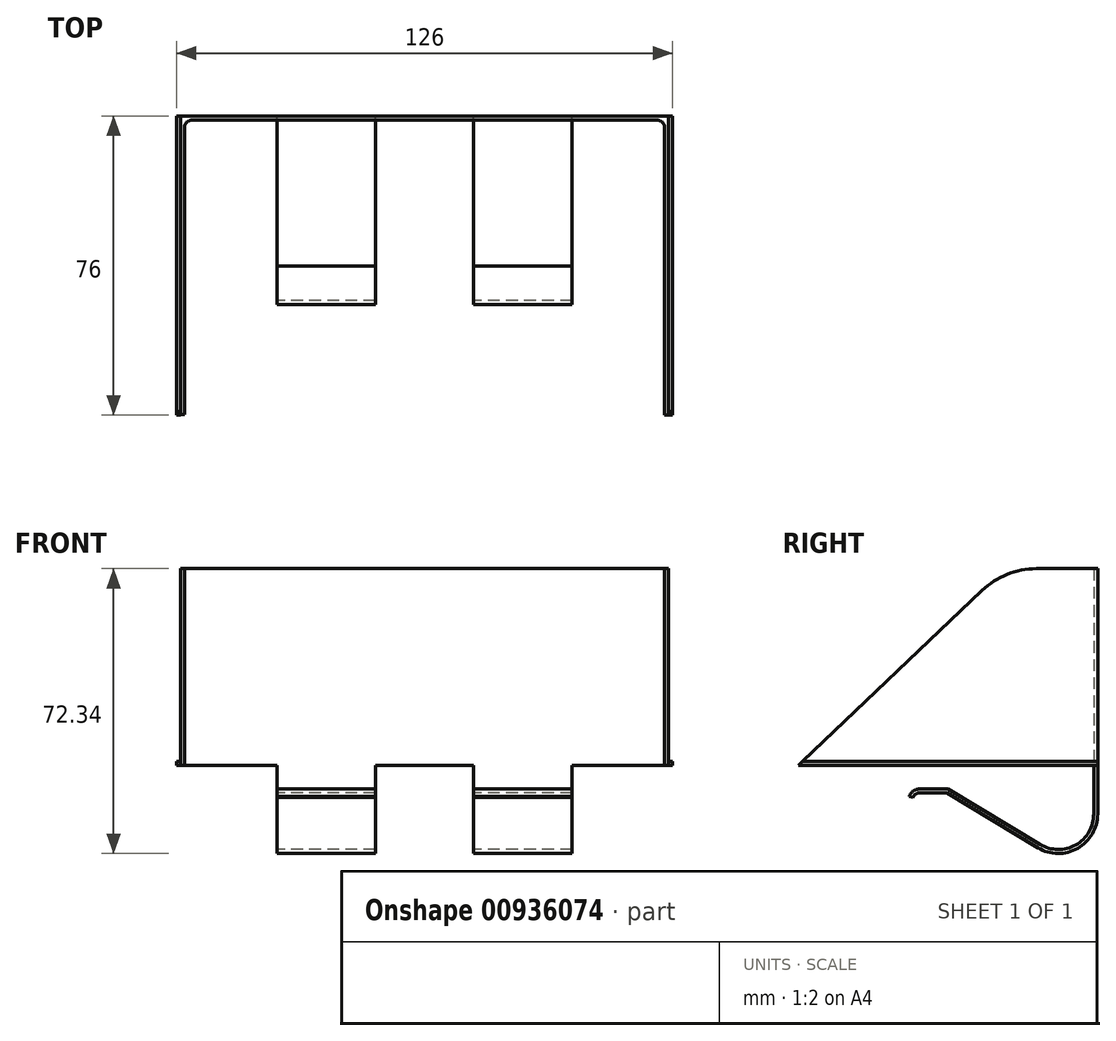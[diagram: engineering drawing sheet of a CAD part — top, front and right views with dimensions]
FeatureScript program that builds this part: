
annotation { "Feature Type Name" : "Feature", "Feature Type Description" : "" }
export const myFeature = defineFeature(function(context is Context, id is Id, definition is map)
    precondition{}
    {
        {
            var Q0;
            Q0=qCreatedBy(makeId("Top.planeOp"),FACE);
            var sketch = newSketch(context, id + "F0", { "sketchPlane" : qUnion([Q0])});
            skLineSegment(sketch, "E0", {"start": v(0, 0) * mm, "end": v(59, 0) * mm});
            skLineSegment(sketch, "E1", {"start": v(0, 0) * mm, "end": v(-59, 0) * mm});
            skLineSegment(sketch, "E2", {"start": v(-61, -2) * mm, "end": v(-61, -75) * mm});
            skLineSegment(sketch, "E3", {"start": v(61, -2) * mm, "end": v(61, -75) * mm});
            skLineSegment(sketch, "E4.0", {"start": v(62, 1) * mm, "end": v(62, -75) * mm});
            skLineSegment(sketch, "E5.0", {"start": v(0, 1) * mm, "end": v(63, 1) * mm});
            skLineSegment(sketch, "E6.0", {"start": v(0, 1) * mm, "end": v(-63, 1) * mm});
            skLineSegment(sketch, "E7.0", {"start": v(-62, 1) * mm, "end": v(-62, -75) * mm});
            skPoint(sketch, "E8.visualSharp", {"position": v(-61, 0) * mm});
            skArc(sketch, "E8.filletArc", {"start": v(-59, 0) * mm, "mid": v(-60.41, -0.59) * mm, "end": v(-61, -2) * mm});
            skPoint(sketch, "E9.visualSharp", {"position": v(61, 0) * mm});
            skArc(sketch, "E9.filletArc", {"start": v(61, -2) * mm, "mid": v(60.41, -0.59) * mm, "end": v(59, 0) * mm});
            skLineSegment(sketch, "E10", {"start": v(61, -75) * mm, "end": v(62, -75) * mm});
            skLineSegment(sketch, "E11", {"start": v(-62, -75) * mm, "end": v(-61, -75) * mm});
            skLineSegment(sketch, "E12", {"start": v(-62, -22.58) * mm, "end": v(-61, -22.58) * mm});
            skLineSegment(sketch, "E13", {"start": v(61, -22.58) * mm, "end": v(62, -22.58) * mm});
            skLineSegment(sketch, "E14", {"start": v(-62, -75) * mm, "end": v(-63, -75) * mm});
            skLineSegment(sketch, "E15", {"start": v(-63, -75) * mm, "end": v(-63, 1) * mm});
            skPoint(sketch, "E16.orphan", {"position": v(-63, 0) * mm});
            skLineSegment(sketch, "E17", {"start": v(62, -75) * mm, "end": v(63, -75) * mm});
            skLineSegment(sketch, "E18", {"start": v(63, -75) * mm, "end": v(63, 1) * mm});
            skPoint(sketch, "E19.orphan", {"position": v(60, 1) * mm});
            skSolve(sketch);
        }
        {
            var Q0;
            Q0=makeQuery(id+"F0.imprint","IMPRINT",FACE,{"disambiguationData":[TD([[makeQuery(id+"F0.imprint","IMPRINT",EDGE,{"derivedFrom":sQuery(id+"F0.wireOp",EDGE,"E0")}),1.0]])]});
            extrude(context, id + "F1", {"entities" : qUnion([Q0]), "depth" : 50 * mm, "offsetDistance" : 25 * mm});
        }
        {
            var Q0;
            Q0=makeQuery(id+"F1.opExtrude","SWEPT_FACE",FACE,{"disambiguationData":[OSD([sQuery(id+"F0.wireOp",EDGE,"E7.0")])]});
            var sketch = newSketch(context, id + "F2", { "sketchPlane" : qUnion([Q0])});
            skLineSegment(sketch, "E20", {"start": v(22.58, 50) * mm, "end": v(74.85, 0) * mm});
            skLineSegment(sketch, "E21", {"start": v(74.85, 0) * mm, "end": v(22.58, 0) * mm});
            skSolve(sketch);
        }
        {
            var Q0;
            Q0=makeQuery(id+"F2.imprint","IMPRINT",FACE,{"disambiguationData":[TD([[makeQuery(id+"F2.imprint","IMPRINT",EDGE,{"derivedFrom":sQuery(id+"F2.wireOp",EDGE,"E20")}),-1.0]])]});
            extrude(context, id + "F3", {"entities" : qUnion([Q0]), "operationType" : NewBodyOperationType.ADD, "oppositeDirection" : true, "depth" : 1 * mm, "offsetDistance" : 25 * mm});
        }
        {
            var Q0;
            Q0=makeQuery(id+"F1.opExtrude","SWEPT_FACE",FACE,{"disambiguationData":[OSD([sQuery(id+"F0.wireOp",EDGE,"E4.0")])]});
            var sketch = newSketch(context, id + "F4", { "sketchPlane" : qUnion([Q0])});
            skLineSegment(sketch, "E22", {"start": v(-22.58, 50) * mm, "end": v(-74.98, 0) * mm});
            skLineSegment(sketch, "E23", {"start": v(-74.98, 0) * mm, "end": v(-22.58, 0) * mm});
            skSolve(sketch);
        }
        {
            var Q0;
            Q0=makeQuery(id+"F4.imprint","IMPRINT",FACE,{"disambiguationData":[TD([[makeQuery(id+"F4.imprint","IMPRINT",EDGE,{"derivedFrom":sQuery(id+"F4.wireOp",EDGE,"E22")}),1.0]])]});
            extrude(context, id + "F5", {"entities" : qUnion([Q0]), "operationType" : NewBodyOperationType.ADD, "oppositeDirection" : true, "depth" : 1 * mm, "offsetDistance" : 25 * mm});
        }
        {
            var Q0;
            {var subQ4=sQuery(id+"F0.wireOp",EDGE,"E17");Q0=makeQuery(id+"F0.imprint","IMPRINT",FACE,{"disambiguationData":[TD([[makeQuery(id+"F0.imprint","IMPRINT",EDGE,{"derivedFrom":subQ4}),1.0]])]});}
            var Q1;
            {var subQ0=sQuery(id+"F0.wireOp",EDGE,"E14");Q1=makeQuery(id+"F0.imprint","IMPRINT",FACE,{"disambiguationData":[TD([[makeQuery(id+"F0.imprint","IMPRINT",EDGE,{"derivedFrom":subQ0}),-1.0]])]});}
            extrude(context, id + "F6", {"entities" : qUnion([Q0, Q1]), "operationType" : NewBodyOperationType.ADD, "depth" : 1 * mm, "offsetDistance" : 25 * mm});
        }
        {
            var Q0;
            Q0=makeQuery(id+"F6.opExtrude","CAP_EDGE",EDGE,{"disambiguationData":[OSD([sQuery(id+"F0.wireOp",EDGE,"E17")])],"isStart":false});
            var Q1;
            Q1=makeQuery(id+"F6.opExtrude","CAP_EDGE",EDGE,{"disambiguationData":[OSD([sQuery(id+"F0.wireOp",EDGE,"E14")])],"isStart":false});
            chamfer(context, id + "F7", {"entities" : qUnion([Q0, Q1]), "width" : 1 * mm, "tangentPropagation" : true});
        }
        {
            var Q0;
            Q0=qCreatedBy(makeId("Right.planeOp"),FACE);
            var sketch = newSketch(context, id + "F8", { "sketchPlane" : qUnion([Q0])});
            skPoint(sketch, "E24.0", {"position": v(1, 0) * mm});
            skLineSegment(sketch, "E25", {"start": v(1, 0) * mm, "end": v(1, -12.34) * mm});
            skLineSegment(sketch, "E26", {"start": v(-37.33, -7) * mm, "end": v(-14.14, -20.91) * mm});
            skPoint(sketch, "E27.visualSharp", {"position": v(1, -30) * mm});
            skArc(sketch, "E27.filletArc", {"start": v(-14.14, -20.91) * mm, "mid": v(-4.07, -21.04) * mm, "end": v(1, -12.34) * mm});
            skLineSegment(sketch, "E28", {"start": v(-37.33, -7) * mm, "end": v(-44.33, -7) * mm});
            skArc(sketch, "E29", {"start": v(-44.33, -7) * mm, "mid": v(-45.3, -7.31) * mm, "end": v(-45.88, -8.14) * mm});
            skArc(sketch, "E30.0", {"start": v(-44.33, -6) * mm, "mid": v(-45.88, -6.5) * mm, "end": v(-46.83, -7.84) * mm});
            skLineSegment(sketch, "E30.1", {"start": v(0, 0) * mm, "end": v(0, -12.34) * mm});
            skArc(sketch, "E30.2", {"start": v(-13.63, -20.06) * mm, "mid": v(-4.57, -20.17) * mm, "end": v(0, -12.34) * mm});
            skLineSegment(sketch, "E30.3", {"start": v(-37.06, -6) * mm, "end": v(-13.63, -20.06) * mm});
            skLineSegment(sketch, "E30.4", {"start": v(-37.06, -6) * mm, "end": v(-44.33, -6) * mm});
            skLineSegment(sketch, "E31", {"start": v(-46.83, -7.84) * mm, "end": v(-45.88, -8.14) * mm});
            skLineSegment(sketch, "E32", {"start": v(0, 0) * mm, "end": v(1, 0) * mm});
            skSolve(sketch);
        }
        {
            var Q0;
            Q0 = qSketchRegion(id + "F8", true);
            extrude(context, id + "F9", {"entities" : qUnion([Q0]), "operationType" : NewBodyOperationType.ADD, "endBound" : BoundingType.SYMMETRIC, "depth" : 75 * mm, "offsetDistance" : 25 * mm});
        }
        {
            var Q0;
            Q0 = qSketchRegion(id + "F8", true);
            extrude(context, id + "F10", {"entities" : qUnion([Q0]), "operationType" : NewBodyOperationType.REMOVE, "endBound" : BoundingType.SYMMETRIC, "oppositeDirection" : true, "depth" : 25 * mm, "offsetDistance" : 25 * mm});
        }
        {
            var Q0;
            {var subQ0=sQuery(id+"F0.wireOp",EDGE,"E12");Q0=makeQuery(id+"F3.boolean.opBoolean","MERGE",EDGE,{"derivedFrom":[makeQuery(id+"F1.opExtrude","CAP_EDGE",EDGE,{"disambiguationData":[OSD([subQ0])],"isStart":false}),makeQuery(id+"F3.opExtrude","SWEPT_EDGE",EDGE,{"disambiguationData":[OSD([sQuery(id+"F0.wireOp",EDGE,"E7.0"),subQ0,sQuery(id+"F2.wireOp",EDGE,"E20")])]})]});}
            var Q1;
            {var subQ0=sQuery(id+"F0.wireOp",EDGE,"E13");Q1=makeQuery(id+"F5.boolean.opBoolean","MERGE",EDGE,{"derivedFrom":[makeQuery(id+"F1.opExtrude","CAP_EDGE",EDGE,{"disambiguationData":[OSD([subQ0])],"isStart":false}),makeQuery(id+"F5.opExtrude","SWEPT_EDGE",EDGE,{"disambiguationData":[OSD([sQuery(id+"F0.wireOp",EDGE,"E4.0"),subQ0,sQuery(id+"F4.wireOp",EDGE,"E22")])]})]});}
            fillet(context, id + "F11", {"entities" : qUnion([Q0, Q1]), "radius" : 20 * mm, "tangentPropagation" : true, "allowEdgeOverflow" : false});
        }
    });
